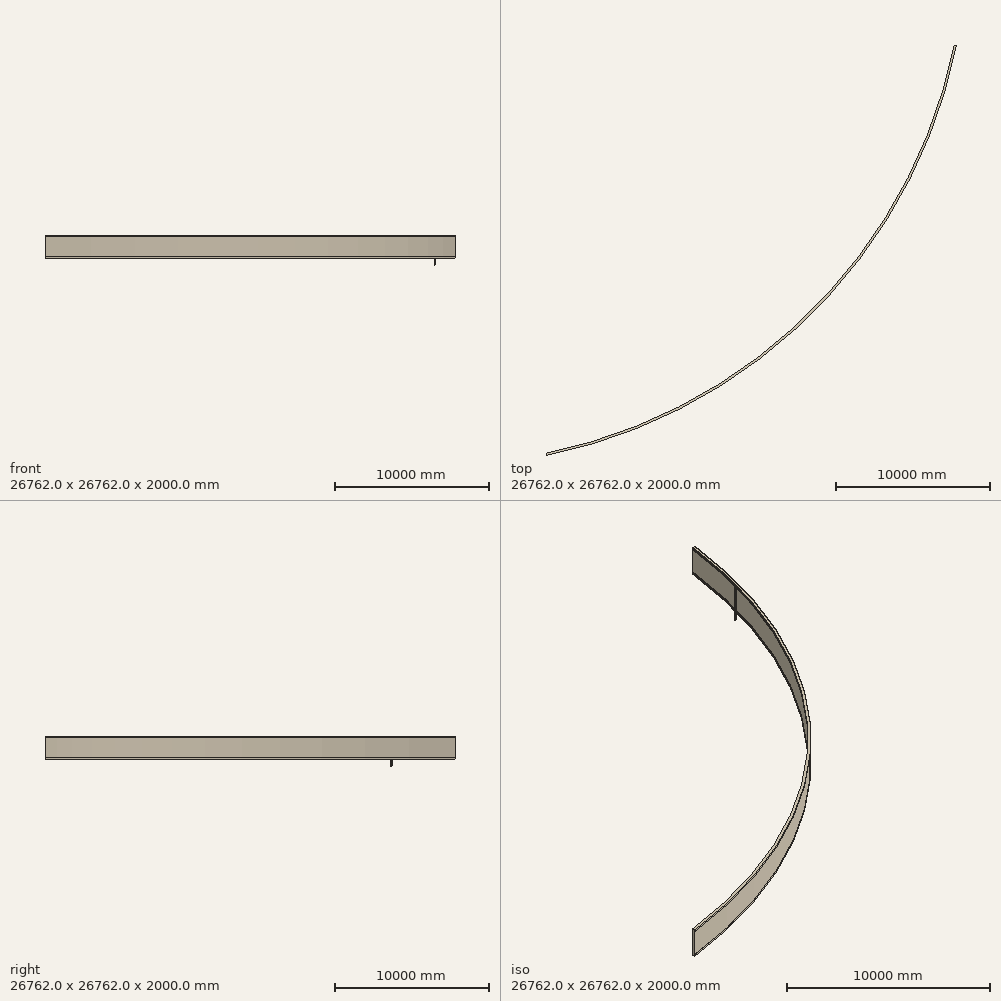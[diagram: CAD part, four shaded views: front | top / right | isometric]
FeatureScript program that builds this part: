
annotation { "Feature Type Name" : "Feature", "Feature Type Description" : "" }
export const myFeature = defineFeature(function(context is Context, id is Id, definition is map)
    precondition{}
    {
        {
            var Q0;
            Q0=qCreatedBy(makeId("Top.planeOp"),FACE);
            var sketch = newSketch(context, id + "F0", { "sketchPlane" : qUnion([Q0])});
            skArc(sketch, "E0", {"start": v(0, -34265) * mm, "mid": v(24229.01, -24229.01) * mm, "end": v(34265, 0) * mm, "construction": true});
            skArc(sketch, "E1", {"start": v(0, -33765) * mm, "mid": v(23875.46, -23875.46) * mm, "end": v(33765, 0) * mm, "construction": true});
            skArc(sketch, "E2", {"start": v(0, -34015) * mm, "mid": v(24052.24, -24052.24) * mm, "end": v(34015, 0) * mm, "construction": true});
            skLineSegment(sketch, "E3", {"start": v(0, 0) * mm, "end": v(34265, 0) * mm, "construction": true});
            skLineSegment(sketch, "E4", {"start": v(34265, 0) * mm, "end": v(0, 0) * mm, "construction": true});
            skLineSegment(sketch, "E5", {"start": v(0, -34265) * mm, "end": v(0, 0) * mm, "construction": true});
            skSolve(sketch);
        }
        {
            var Q0;
            Q0=qCreatedBy(makeId("Right.planeOp"),FACE);
            var sketch = newSketch(context, id + "F1", { "sketchPlane" : qUnion([Q0])});
            skPoint(sketch, "E6.0", {"position": v(0, 0) * mm});
            skLineSegment(sketch, "E7", {"start": v(0, 0) * mm, "end": v(0, 7479.54) * mm, "construction": true});
            skSolve(sketch);
        }
        {
            var Q0;
            Q0=qCreatedBy(makeId("Top.planeOp"),FACE);
            var sketch = newSketch(context, id + "F2", { "sketchPlane" : qUnion([Q0])});
            skLineSegment(sketch, "E8", {"start": v(0, 0) * mm, "end": v(37045.14, -12467.07) * mm, "construction": true});
            skArc(sketch, "E9.0", {"start": v(0, -34015) * mm, "mid": v(24052.24, -24052.24) * mm, "end": v(34015, 0) * mm, "construction": true});
            skArc(sketch, "E10.0", {"start": v(0, -34265) * mm, "mid": v(24229.01, -24229.01) * mm, "end": v(34265, 0) * mm, "construction": true});
            skArc(sketch, "E11.0", {"start": v(0, -33765) * mm, "mid": v(23875.46, -23875.46) * mm, "end": v(33765, 0) * mm, "construction": true});
            skLineSegment(sketch, "E12", {"start": v(32096.18, -10801.56) * mm, "end": v(32112.13, -10754.17) * mm, "construction": true});
            skLineSegment(sketch, "E13", {"start": v(32112.13, -10754.17) * mm, "end": v(32254.3, -10802.01) * mm, "construction": true});
            skLineSegment(sketch, "E14", {"start": v(32222.4, -10896.79) * mm, "end": v(32080.23, -10848.95) * mm, "construction": true});
            skLineSegment(sketch, "E15", {"start": v(32080.23, -10848.95) * mm, "end": v(32096.18, -10801.56) * mm, "construction": true});
            skLineSegment(sketch, "E16", {"start": v(32254.3, -10802.01) * mm, "end": v(32238.34, -10849.4) * mm, "construction": true});
            skLineSegment(sketch, "E17", {"start": v(32238.34, -10849.4) * mm, "end": v(32222.4, -10896.79) * mm, "construction": true});
            skLineSegment(sketch, "E18", {"start": v(32222.4, -10896.79) * mm, "end": v(32151.31, -10872.87) * mm});
            skLineSegment(sketch, "E19", {"start": v(32151.31, -10872.87) * mm, "end": v(32149.4, -10878.55) * mm});
            skLineSegment(sketch, "E20", {"start": v(32222.4, -10896.79) * mm, "end": v(32198.47, -10967.87) * mm});
            skLineSegment(sketch, "E21", {"start": v(32198.47, -10967.87) * mm, "end": v(32192.79, -10965.96) * mm});
            skLineSegment(sketch, "E22", {"start": v(32192.79, -10965.96) * mm, "end": v(32214.8, -10900.56) * mm});
            skLineSegment(sketch, "E23", {"start": v(32149.4, -10878.55) * mm, "end": v(32214.8, -10900.56) * mm});
            skSolve(sketch);
        }
        {
            var Q0;
            Q0=qSketchRegion(id+"F2",true);
            extrude(context, id + "F3", {"entities" : qUnion([Q0]), "depth" : 1500 * mm, "hasSecondDirection" : true, "secondDirectionOppositeDirection" : true, "secondDirectionDepth" : 500 * mm});
        }
        {
            var Q0;
            Q0=makeQuery(id+"F3.opExtrude","SWEPT_FACE",FACE,{"disambiguationData":[OSD([sQuery(id+"F2.wireOp",EDGE,"E23")])]});
            var sketch = newSketch(context, id + "F4", { "sketchPlane" : qUnion([Q0])});
            skLineSegment(sketch, "E24", {"start": v(33977.5, -561.93) * mm, "end": v(33977.5, 72.11) * mm, "construction": true});
            skLineSegment(sketch, "E25.0", {"start": v(33940, 1500) * mm, "end": v(33940, -500) * mm, "construction": true});
            skCircle(sketch, "E26", {"center": v(33977.5, -100) * mm, "radius": 12.5 * mm});
            skCircle(sketch, "E27", {"center": v(33977.5, -400) * mm, "radius": 12.5 * mm});
            skSolve(sketch);
        }
        {
            var Q0;
            Q0 = qSketchRegion(id + "F4", true);
            extrude(context, id + "F5", {"entities" : qUnion([Q0]), "operationType" : NewBodyOperationType.REMOVE, "oppositeDirection" : true, "depth" : 25 * mm});
        }
        {
            var Q0;
            Q0=qCreatedBy(makeId("Front.planeOp"),FACE);
            var sketch = newSketch(context, id + "F6", { "sketchPlane" : qUnion([Q0])});
            skLineSegment(sketch, "E28", {"start": v(34035, 0) * mm, "end": v(34185, 0) * mm});
            skLineSegment(sketch, "E29", {"start": v(34185, 100) * mm, "end": v(34185, 0) * mm});
            skLineSegment(sketch, "E30", {"start": v(34185, 100) * mm, "end": v(34179, 100) * mm});
            skLineSegment(sketch, "E31", {"start": v(34179, 6) * mm, "end": v(34179, 100) * mm});
            skLineSegment(sketch, "E32", {"start": v(34179, 6) * mm, "end": v(34041, 6) * mm});
            skLineSegment(sketch, "E33", {"start": v(34041, 100) * mm, "end": v(34041, 6) * mm});
            skLineSegment(sketch, "E34", {"start": v(34035, 100) * mm, "end": v(34035, 0) * mm});
            skLineSegment(sketch, "E35", {"start": v(34035, 100) * mm, "end": v(34041, 100) * mm});
            skLineSegment(sketch, "E36", {"start": v(34035, 1500) * mm, "end": v(34185, 1500) * mm});
            skLineSegment(sketch, "E37", {"start": v(34185, 1500) * mm, "end": v(34185, 1400) * mm});
            skLineSegment(sketch, "E38", {"start": v(34185, 1400) * mm, "end": v(34179, 1400) * mm});
            skLineSegment(sketch, "E39", {"start": v(34179, 1400) * mm, "end": v(34179, 1494) * mm});
            skLineSegment(sketch, "E40", {"start": v(34179, 1494) * mm, "end": v(34041, 1494) * mm});
            skLineSegment(sketch, "E41", {"start": v(34041, 1494) * mm, "end": v(34041, 1400) * mm});
            skLineSegment(sketch, "E42", {"start": v(34035, 1500) * mm, "end": v(34035, 1400) * mm});
            skLineSegment(sketch, "E43", {"start": v(34035, 1400) * mm, "end": v(34041, 1400) * mm});
            skSolve(sketch);
        }
        {
            var Q0;
            Q0 = qSketchRegion(id + "F6", true);
            var Q1;
            Q1=sQuery(id+"F1.wireOp",EDGE,"E7");
            revolve(context, id + "F7", {"entities" : qUnion([Q0]), "axis" : qUnion([Q1]), "revolveType" : RevolveType.ONE_DIRECTION, "oppositeDirection" : true, "angle" : 90 * degree});
        }
        {
            var Q0;
            Q0=qCreatedBy(makeId("Front.planeOp"),FACE);
            var sketch = newSketch(context, id + "F8", { "sketchPlane" : qUnion([Q0])});
            skLineSegment(sketch, "E44.0", {"start": v(34179, 1400) * mm, "end": v(34179, 1494) * mm, "construction": true});
            skLineSegment(sketch, "E45.0", {"start": v(34179, 1494) * mm, "end": v(34041, 1494) * mm, "construction": true});
            skPoint(sketch, "E46.0", {"position": v(34041, 1447) * mm});
            skLineSegment(sketch, "E47.0", {"start": v(34041, 1494) * mm, "end": v(34041, 1400) * mm, "construction": true});
            skLineSegment(sketch, "E48.0", {"start": v(34041, 100) * mm, "end": v(34041, 6) * mm, "construction": true});
            skLineSegment(sketch, "E49.0", {"start": v(34179, 6) * mm, "end": v(34041, 6) * mm, "construction": true});
            skPoint(sketch, "E50.0", {"position": v(34179, 53) * mm});
            skLineSegment(sketch, "E51.0", {"start": v(34179, 6) * mm, "end": v(34179, 100) * mm, "construction": true});
            skLineSegment(sketch, "E52", {"start": v(34110, -101.67) * mm, "end": v(34110, 16) * mm, "construction": true});
            skLineSegment(sketch, "E53.bottom", {"start": v(34110, 1484) * mm, "end": v(34045, 1484) * mm});
            skLineSegment(sketch, "E53.top", {"start": v(34110, 16) * mm, "end": v(34045, 16) * mm});
            skLineSegment(sketch, "E53.right", {"start": v(34045, 1484) * mm, "end": v(34045, 16) * mm});
            skLineSegment(sketch, "E54.bottom", {"start": v(34110, 16) * mm, "end": v(34175, 16) * mm});
            skLineSegment(sketch, "E54.top", {"start": v(34110, 1484) * mm, "end": v(34175, 1484) * mm});
            skLineSegment(sketch, "E54.right", {"start": v(34175, 16) * mm, "end": v(34175, 1484) * mm});
            skLineSegment(sketch, "E55.trimOffspring", {"start": v(34110, 1484) * mm, "end": v(34110, 1811.81) * mm, "construction": true});
            skSolve(sketch);
        }
        {
            var Q0;
            Q0 = qSketchRegion(id + "F8", true);
            var Q1;
            Q1=sQuery(id+"F1.wireOp",EDGE,"E7");
            revolve(context, id + "F9", {"entities" : qUnion([Q0]), "axis" : qUnion([Q1]), "revolveType" : RevolveType.ONE_DIRECTION, "oppositeDirection" : true, "angle" : 90 * degree});
        }
        {
            var Q0;
            Q0=qCreatedBy(makeId("Front.planeOp"),FACE);
            var sketch = newSketch(context, id + "F10", { "sketchPlane" : qUnion([Q0])});
            skPoint(sketch, "E56.0", {"position": v(0, 3739.77) * mm});
            skLineSegment(sketch, "E57.0", {"start": v(0, 0) * mm, "end": v(0, 7479.54) * mm, "construction": true});
            skLineSegment(sketch, "E58.top", {"start": v(0, 4000) * mm, "end": v(6750, 4000) * mm});
            skLineSegment(sketch, "E58.left", {"start": v(0, 0) * mm, "end": v(0, 4000) * mm});
            skLineSegment(sketch, "E58.right", {"start": v(6750, 0) * mm, "end": v(6750, 4000) * mm});
            skLineSegment(sketch, "E59.top", {"start": v(0, -3899.49) * mm, "end": v(6750, -3899.49) * mm});
            skLineSegment(sketch, "E59.left", {"start": v(0, 0) * mm, "end": v(0, -3899.49) * mm});
            skLineSegment(sketch, "E59.right", {"start": v(6750, 0) * mm, "end": v(6750, -3899.49) * mm});
            skSolve(sketch);
        }
        {
            var Q0;
            Q0=makeQuery(id+"F10.imprint","IMPRINT",FACE,{"disambiguationData":[TD([[makeQuery(id+"F10.imprint","IMPRINT",EDGE,{"derivedFrom":sQuery(id+"F10.wireOp",EDGE,"E58.top")}),-1.0]])]});
            extrude(context, id + "F11", {"entities" : qUnion([Q0]), "operationType" : NewBodyOperationType.REMOVE, "endBound" : BoundingType.THROUGH_ALL, "depth" : 25 * mm});
        }
        {
            var Q0;
            Q0=qCreatedBy(makeId("Right.planeOp"),FACE);
            var sketch = newSketch(context, id + "F12", { "sketchPlane" : qUnion([Q0])});
            skLineSegment(sketch, "E60.0", {"start": v(0, 0) * mm, "end": v(0, 7479.54) * mm, "construction": true});
            skLineSegment(sketch, "E61.top", {"start": v(0, 4000) * mm, "end": v(-6750, 4000) * mm});
            skLineSegment(sketch, "E61.left", {"start": v(0, 0) * mm, "end": v(0, 4000) * mm});
            skLineSegment(sketch, "E61.right", {"start": v(-6750, 0) * mm, "end": v(-6750, 4000) * mm});
            skLineSegment(sketch, "E62.top", {"start": v(0, -4000) * mm, "end": v(-6750, -4000) * mm});
            skLineSegment(sketch, "E62.left", {"start": v(0, 0) * mm, "end": v(0, -4000) * mm});
            skLineSegment(sketch, "E62.right", {"start": v(-6750, 0) * mm, "end": v(-6750, -4000) * mm});
            skSolve(sketch);
        }
        {
            var Q0;
            Q0 = qSketchRegion(id + "F12", true);
            extrude(context, id + "F13", {"entities" : qUnion([Q0]), "operationType" : NewBodyOperationType.REMOVE, "endBound" : BoundingType.THROUGH_ALL, "depth" : 25 * mm});
        }
    });
